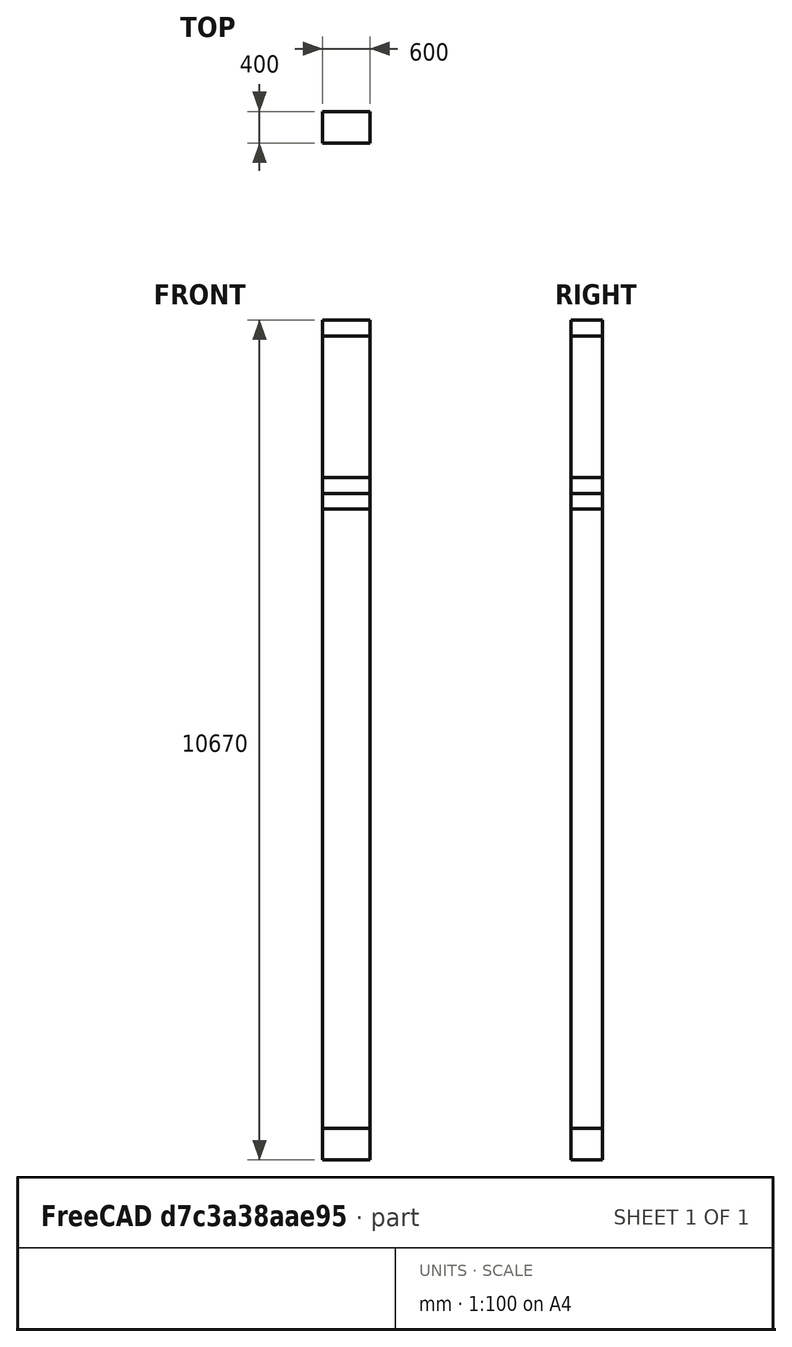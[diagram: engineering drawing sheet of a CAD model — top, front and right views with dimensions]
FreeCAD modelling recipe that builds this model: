
FCSTD DOCUMENT  (FreeCAD 0.21R33694 (Git))
Label: column_3_no_mast
License: All rights reserved
LicenseURL: http://en.wikipedia.org/wiki/All_rights_reserved
objects: Part::FeaturePython×10, Part::Feature×7, Part::Plane×5, Fem::ConstraintForce×4, Fem::ConstraintFixed×2, Fem::FemSolverObjectPython×1, App::MaterialObjectPython×1, Part::Box×1, Fem::FeaturePython×1, Fem::FemMeshObjectPython×1, Fem::FemAnalysis×1
note: 23 computed .brp shape members not serialized (recipe doc carries the construction recipe); baked Part::Feature solids carry a one-line shape summary decoded from their .brp

FEATURE [Fem::FemSolverObjectPython] SolverCcxTools  # FEM object (typed FeaturePython)
  AnalysisType = 0
  BeamShellResultOutput3D = true
  BucklingFactors = 1
  EigenmodeHighLimit = 1000000
  EigenmodeLowLimit = 0
  EigenmodesCount = 10
  GeometricalNonlinearity = 0
  IterationsControlParameterCutb = 0.25,0.5,0.75,0.85,,,1.5,
  IterationsControlParameterIter = 4,8,9,200,10,400,,200,,
  IterationsControlParameterTimeUse = false
  IterationsThermoMechMaximum = 2000
  IterationsUserDefinedIncrementations = false
  IterationsUserDefinedTimeStepLength = false
  MaterialNonlinearity = 0
  MatrixSolverType = 0
  SplitInputWriter = true
  ThermoMechSteadyState = true
  TimeEnd = 1
  TimeInitialStep = 0.01
FEATURE [App::MaterialObjectPython] MaterialSolid  label="B450"  # material (typed FeaturePython)
  Category = 0
  Material = AngleOfFriction=30 deg,AuthorAndLicense=(c) 2019 Bernd Hahnebach (CC-BY 3.0),CardName=Concrete-EN-C35_45,CompressiveStrength=15.75 MPa,+7 more (map truncated)
FEATURE [Fem::ConstraintFixed] ConstraintFixed  label="support"
  NormalDirection = (0,0,-1)
FEATURE [Part::Box] Box  label="Cube"
  AttacherType = Attacher::AttachEngine3D
  Height = 10670
  Length = 600
  Width = 400
FEATURE [Part::Plane] Plane
  AttacherType = Attacher::AttachEngine3D
  Length = 600
  Placement = pos=(0,0,8270) rot=(0,0,1;0rad)
  Width = 400
FEATURE [Part::Plane] Plane002
  AttacherType = Attacher::AttachEngine3D
  Length = 600
  Placement = pos=(0,0,8470) rot=(0,0,1;0rad)
  Width = 400
FEATURE [Part::Plane] Plane003
  AttacherType = Attacher::AttachEngine3D
  Length = 600
  Placement = pos=(0,0,8670) rot=(0,0,1;0rad)
  Width = 400
FEATURE [Part::Plane] Plane004
  AttacherType = Attacher::AttachEngine3D
  Length = 600
  Placement = pos=(0,0,10470) rot=(0,0,1;0rad)
  Width = 400
FEATURE [Part::FeaturePython] Slice  # WARN: FeaturePython — macro-defined, semantics opaque (R4)
  Base = -> Box
  Mode = 1
  Tolerance = 0
  Tools = -> [Plane,Plane002,Plane003,Plane004]
FEATURE [Part::FeaturePython] Slice_child0  label="Slice.0"  # WARN: FeaturePython — macro-defined, semantics opaque (R4)
  Base = -> Slice
  FilterType = 1
  Invert = false
  OverrideMaxVal = 0
  WindowFrom = 80
  WindowTo = 100
  items = 0
FEATURE [Part::FeaturePython] Slice_child1  label="Slice.1"  # WARN: FeaturePython — macro-defined, semantics opaque (R4)
  Base = -> Slice
  FilterType = 1
  Invert = false
  OverrideMaxVal = 0
  WindowFrom = 80
  WindowTo = 100
  items = 1
FEATURE [Fem::ConstraintForce] ConstraintForce004  label="crane_V2(p)"
  Direction = -> Slice_child1 [Edge3]
  DirectionVector = (0,0,1)
  Force = 250000
  NormalDirection = (-1,0,0)
  Points = (16) [(0,400,8270),(0,400,8336.67),(0,400,8403.33),(0,400,8470),(0,266.667,8270),(0,266.667,8336.67),(0,266.667,8403.33),(0,266.667,8470),(0,133.333,8270),+7 more]
  References = -> [Slice_child1]
  Scale = 19
FEATURE [Part::FeaturePython] Slice_child2  label="Slice.2"  # WARN: FeaturePython — macro-defined, semantics opaque (R4)
  Base = -> Slice
  FilterType = 1
  Invert = false
  OverrideMaxVal = 0
  WindowFrom = 80
  WindowTo = 100
  items = 2
FEATURE [Fem::ConstraintForce] ConstraintForce003  label="crane_V1(p)"
  Direction = -> Slice_child2 [Edge5]
  DirectionVector = (0,0,-1)
  Force = 550000
  NormalDirection = (1,0,0)
  Points = (16) [(600,400,8270),(600,400,8336.67),(600,400,8403.33),(600,400,8470),(600,266.667,8270),(600,266.667,8336.67),(600,266.667,8403.33),(600,266.667,8470),+8 more]
  References = -> [Slice_child1]
  Reversed = true
  Scale = 19
FEATURE [Part::FeaturePython] Slice_child3  label="Slice.3"  # WARN: FeaturePython — macro-defined, semantics opaque (R4)
  Base = -> Slice
  FilterType = 1
  Invert = false
  OverrideMaxVal = 0
  WindowFrom = 80
  WindowTo = 100
  items = 3
FEATURE [Part::FeaturePython] Slice_child4  label="Slice.4"  # WARN: FeaturePython — macro-defined, semantics opaque (R4)
  Base = -> Slice
  FilterType = 1
  Invert = false
  OverrideMaxVal = 0
  WindowFrom = 80
  WindowTo = 100
  items = 4
FEATURE [Fem::ConstraintForce] ConstraintForce  label="wind"
  DirectionVector = (1,0,0)
  Force = 51200
  NormalDirection = (-1,0,0)
  Points = (132) [(0,400,10470),(0,400,10536.7),(0,400,10603.3),(0,400,10670),(0,266.667,10470),(0,266.667,10536.7),(0,266.667,10603.3),(0,266.667,10670),+124 more]
  References = -> [Slice_child4,Slice_child3,Slice_child2,Slice_child1,Slice_child0]
  Reversed = true
  Scale = 59
FEATURE [Fem::ConstraintForce] ConstraintForce002  label="roof_girder_R(p)"
  DirectionVector = (0,0,-1)
  Force = 100000
  NormalDirection = (0,0,1)
  Points = (16) [(0,0,10670),(200,0,10670),(400,0,10670),(600,0,10670),(0,133.333,10670),(200,133.333,10670),(400,133.333,10670),(600,133.333,10670),(0,266.667,10670),+7 more]
  References = -> [Slice_child4]
  Reversed = true
  Scale = 24
FEATURE [Part::Feature] Solid001
  shape: bbox 600 x 400 x 200 mm, 6 faces (baked)
FEATURE [Part::Feature] Solid002
  shape: bbox 600 x 400 x 200 mm, 6 faces (baked)
FEATURE [Part::Feature] Solid003
  shape: bbox 600 x 400 x 1800 mm, 6 faces (baked)
FEATURE [Part::Feature] Solid004
  shape: bbox 600 x 400 x 200 mm, 6 faces (baked)
FEATURE [Fem::ConstraintFixed] ConstraintFixed001  label="foundation"
  NormalDirection = (0,0,-1)
  Normals = (16) [(0,0,-1),(0,0,-1),(0,0,-1),(0,0,-1),(0,0,-1),(0,0,-1),(0,0,-1),(0,0,-1),(0,0,-1),(0,0,-1),(0,0,-1),(0,0,-1),(0,0,-1),(0,0,-1),(0,0,-1),(0,0,-1)]
  Points = (16) [(0,0,0),(200,0,0),(400,0,0),(600,0,0),(0,133.333,0),(200,133.333,0),(400,133.333,0),(600,133.333,0),(0,266.667,0),(200,266.667,0),(400,266.667,0),+5 more]
  References = -> [Slice_child0]
  Scale = 24
FEATURE [Part::Plane] Plane005
  AttacherType = Attacher::AttachEngine3D
  Length = 600
  Placement = pos=(0,0,400) rot=(0,0,1;0rad)
  Width = 400
FEATURE [Part::Feature] Solid005
  shape: bbox 600 x 400 x 8270 mm, 6 faces (baked)
FEATURE [Part::FeaturePython] Slice001  # WARN: FeaturePython — macro-defined, semantics opaque (R4)
  Base = -> Solid005
  Mode = 1
  Tolerance = 0
  Tools = -> [Plane005]
FEATURE [Part::FeaturePython] Slice001_child0  label="Slice001.0"  # WARN: FeaturePython — macro-defined, semantics opaque (R4)
  Base = -> Slice001
  FilterType = 1
  Invert = false
  OverrideMaxVal = 0
  WindowFrom = 80
  WindowTo = 100
  items = 0
FEATURE [Part::FeaturePython] Slice001_child1  label="Slice001.1"  # WARN: FeaturePython — macro-defined, semantics opaque (R4)
  Base = -> Slice001
  FilterType = 1
  Invert = false
  OverrideMaxVal = 0
  WindowFrom = 80
  WindowTo = 100
  items = 1
FEATURE [Part::Feature] Solid006
  shape: bbox 600 x 400 x 400 mm, 6 faces (baked)
FEATURE [Part::Feature] Solid007
  shape: bbox 600 x 400 x 7870 mm, 6 faces (baked)
FEATURE [Part::FeaturePython] BooleanFragments  # WARN: FeaturePython — macro-defined, semantics opaque (R4)
  Mode = 0
  Objects = -> [Solid001,Solid002,Solid003,Solid004,Solid006,Solid007]
  Tolerance = 0
FEATURE [Fem::FeaturePython] MeshRegion  # FEM object (typed FeaturePython)
  CharacteristicLength = 50
  References = -> [BooleanFragments]
FEATURE [Fem::FemMeshObjectPython] FEMMeshGmsh  # FEM object (typed FeaturePython)
  Algorithm2D = 0
  Algorithm3D = 0
  CharacteristicLengthMax = 1000
  CharacteristicLengthMin = 0
  CoherenceMesh = true
  ElementDimension = 0
  ElementOrder = 1
  GeometryTolerance = 1e-06
  GroupsOfNodes = false
  HighOrderOptimize = 0
  MeshRegionList = -> [MeshRegion]
  MeshSizeFromCurvature = 12
  OptimizeNetgen = false
  OptimizeStd = true
  Part = -> BooleanFragments
  RecombinationAlgorithm = 0
  Recombine3DAll = false
  RecombineAll = false
  SecondOrderLinear = false
FEATURE [Fem::FemAnalysis] Analysis
  Group = -> [SolverCcxTools,MaterialSolid,ConstraintForce,ConstraintForce002,ConstraintFixed,ConstraintForce003,ConstraintForce004,ConstraintFixed001,FEMMeshGmsh]
